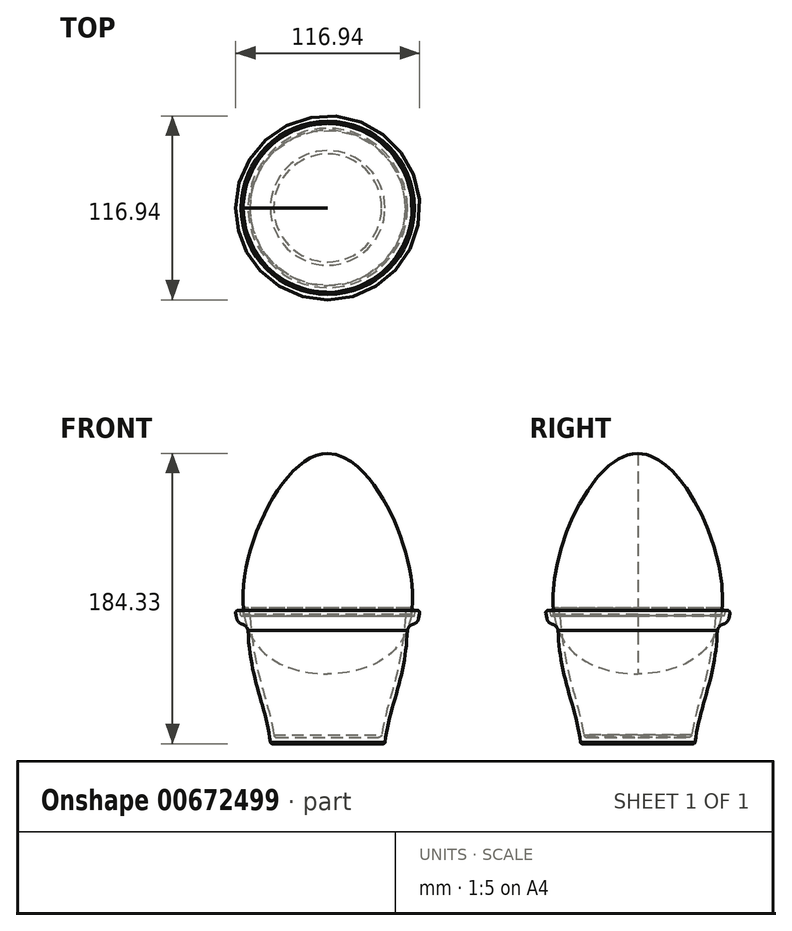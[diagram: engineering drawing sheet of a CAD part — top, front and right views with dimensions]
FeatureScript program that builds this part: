
annotation { "Feature Type Name" : "Feature", "Feature Type Description" : "" }
export const myFeature = defineFeature(function(context is Context, id is Id, definition is map)
    precondition{}
    {
        {
            var Q0;
            Q0=qCreatedBy(makeId("Front.planeOp"),FACE);
            var sketch = newSketch(context, id + "F0", { "sketchPlane" : qUnion([Q0])});
            skLineSegment(sketch, "E0", {"start": v(0, 0) * mm, "end": v(-47.5, 0) * mm});
            skLineSegment(sketch, "E1", {"start": v(-47.5, 0) * mm, "end": v(-32.5, -75) * mm});
            skLineSegment(sketch, "E2", {"start": v(-32.5, -75) * mm, "end": v(0, -75) * mm});
            skLineSegment(sketch, "E3", {"start": v(0, -75) * mm, "end": v(0, 0) * mm});
            skLineSegment(sketch, "E4.MirrorCS", {"start": v(0, 0) * mm, "end": v(47.5, 0) * mm});
            skLineSegment(sketch, "E5.MirrorCS", {"start": v(47.5, 0) * mm, "end": v(32.5, -75) * mm});
            skLineSegment(sketch, "E6.MirrorCS", {"start": v(32.5, -75) * mm, "end": v(0, -75) * mm});
            skSolve(sketch);
        }
        {
            var Q0;
            Q0=qCreatedBy(makeId("Front.planeOp"),FACE);
            var sketch = newSketch(context, id + "F1", { "sketchPlane" : qUnion([Q0])});
            skFitSpline(sketch, "E7", {"points": [v(0, 102.33) * mm, v(-53.18, 0) * mm, v(0, -37.67) * mm, v(53.18, 0) * mm, v(0, 102.33) * mm]});
            skLineSegment(sketch, "E8", {"start": v(-53.18, 0) * mm, "end": v(0, 0) * mm});
            skLineSegment(sketch, "E9", {"start": v(0, 102.33) * mm, "end": v(0, 0) * mm});
            skFitSpline(sketch, "E10", {"points": [v(-53.18, 0) * mm, v(0, -37.67) * mm, v(53.18, 0) * mm, v(0, 102.33) * mm, v(-53.18, 0) * mm]});
            skLineSegment(sketch, "E11", {"start": v(0, 0) * mm, "end": v(0, -37.67) * mm});
            skSolve(sketch);
        }
        {
            var Q0;
            Q0=qCreatedBy(makeId("Front.planeOp"),FACE);
            var sketch = newSketch(context, id + "F2", { "sketchPlane" : qUnion([Q0])});
            skLineSegment(sketch, "E12", {"start": v(-56.56, 2.58) * mm, "end": v(-56.97, 2.58) * mm});
            skLineSegment(sketch, "E13", {"start": v(-58.44, 0.79) * mm, "end": v(-57.82, -2.32) * mm});
            skLineSegment(sketch, "E14", {"start": v(-55.55, -6) * mm, "end": v(-54.6, -6) * mm});
            skLineSegment(sketch, "E15", {"start": v(-35.38, -82) * mm, "end": v(0, -82) * mm});
            skLineSegment(sketch, "E16", {"start": v(0, -82) * mm, "end": v(0, 0) * mm});
            skLineSegment(sketch, "E17", {"start": v(-55.58, 1.78) * mm, "end": v(-55.02, -1) * mm});
            skLineSegment(sketch, "E18", {"start": v(-55.02, -1) * mm, "end": v(-49.34, -1) * mm});
            skLineSegment(sketch, "E19", {"start": v(-32.3, -78) * mm, "end": v(0, -78) * mm});
            skPoint(sketch, "E20.visualSharp", {"position": v(-51.4, -6) * mm});
            skArc(sketch, "E20.filletArc", {"start": v(-50.6, -10.02) * mm, "mid": v(-51.85, -7.58) * mm, "end": v(-54.2, -6.17) * mm});
            skArc(sketch, "E21.filletArc", {"start": v(-57.82, -2.32) * mm, "mid": v(-56.56, -4.76) * mm, "end": v(-54.2, -6.17) * mm});
            skPoint(sketch, "E22.visualSharp", {"position": v(-36.2, -82) * mm});
            skArc(sketch, "E22.filletArc", {"start": v(-36.36, -81.2) * mm, "mid": v(-36.01, -81.77) * mm, "end": v(-35.38, -82) * mm});
            skPoint(sketch, "E23.visualSharp", {"position": v(-33.94, -78) * mm});
            skArc(sketch, "E23.filletArc", {"start": v(-34.26, -76.4) * mm, "mid": v(-33.57, -77.55) * mm, "end": v(-32.3, -78) * mm});
            skPoint(sketch, "E24.visualSharp", {"position": v(-58.8, 2.58) * mm});
            skArc(sketch, "E24.filletArc", {"start": v(-56.97, 2.58) * mm, "mid": v(-58.13, 2.03) * mm, "end": v(-58.44, 0.79) * mm});
            skPoint(sketch, "E25.visualSharp", {"position": v(-55.74, 2.58) * mm});
            skArc(sketch, "E25.filletArc", {"start": v(-55.58, 1.78) * mm, "mid": v(-55.93, 2.36) * mm, "end": v(-56.56, 2.58) * mm});
            skFitSpline(sketch, "E26", {"points": [v(-50.6, -10.02) * mm, v(-36.36, -81.2) * mm], "startDerivative": vector(3.36, -91.43) * mm, "endDerivative": vector(9.55, -72.68) * mm});
            skFitSpline(sketch, "E27", {"points": [v(-49.34, -1) * mm, v(-34.26, -76.4) * mm], "startDerivative": vector(8.58, -116.03) * mm, "endDerivative": vector(12.2, -75.01) * mm});
            skSolve(sketch);
        }
        {
            var Q0;
            Q0=makeQuery(id+"F2.imprint","IMPRINT",FACE,{"disambiguationData":[TD([[makeQuery(id+"F2.imprint","IMPRINT",EDGE,{"derivedFrom":sQuery(id+"F2.wireOp",EDGE,"E12")}),1.0]])]});
            var Q1;
            Q1=sQuery(id+"F0.wireOp",EDGE,"E3");
            revolve(context, id + "F3", {"entities" : qUnion([Q0]), "axis" : qUnion([Q1]), "revolveType" : RevolveType.FULL});
        }
        {
            var Q0;
            {var subQ0=sQuery(id+"F1.wireOp",EDGE,"E8");Q0=makeQuery(id+"F1.imprint","IMPRINT",FACE,{"disambiguationData":[TD([[makeQuery(id+"F1.imprint","IMPRINT",EDGE,{"derivedFrom":subQ0}),1.0]])]});}
            var Q1;
            {var subQ0=sQuery(id+"F1.wireOp",EDGE,"E8");Q1=makeQuery(id+"F1.imprint","IMPRINT",FACE,{"disambiguationData":[TD([[makeQuery(id+"F1.imprint","IMPRINT",EDGE,{"derivedFrom":subQ0}),-1.0]])]});}
            var Q2;
            Q2=sQuery(id+"F1.wireOp",EDGE,"E9");
            revolve(context, id + "F4", {"entities" : qUnion([Q0, Q1]), "axis" : qUnion([Q2]), "revolveType" : RevolveType.FULL});
        }
        {
            var Q0;
            Q0=qCreatedBy(makeId("Front.planeOp"),FACE);
            var sketch = newSketch(context, id + "F5", { "sketchPlane" : qUnion([Q0])});
            skLineSegment(sketch, "E28", {"start": v(-54.02, 3.23) * mm, "end": v(-53.42, -0.2) * mm});
            skLineSegment(sketch, "E29", {"start": v(-52.68, -0.82) * mm, "end": v(-50.2, -0.82) * mm});
            skLineSegment(sketch, "E30", {"start": v(-49.46, 0.06) * mm, "end": v(-50.06, 3.49) * mm});
            skLineSegment(sketch, "E31", {"start": v(-50.8, 4.1) * mm, "end": v(-53.28, 4.1) * mm});
            skPoint(sketch, "E32.visualSharp", {"position": v(-54.17, 4.1) * mm});
            skArc(sketch, "E32.filletArc", {"start": v(-53.28, 4.1) * mm, "mid": v(-53.85, 3.84) * mm, "end": v(-54.02, 3.23) * mm});
            skPoint(sketch, "E33.visualSharp", {"position": v(-50.17, 4.1) * mm});
            skArc(sketch, "E33.filletArc", {"start": v(-50.06, 3.49) * mm, "mid": v(-50.32, 3.93) * mm, "end": v(-50.8, 4.1) * mm});
            skPoint(sketch, "E34.visualSharp", {"position": v(-53.31, -0.82) * mm});
            skArc(sketch, "E34.filletArc", {"start": v(-53.42, -0.2) * mm, "mid": v(-53.16, -0.64) * mm, "end": v(-52.68, -0.82) * mm});
            skPoint(sketch, "E35.visualSharp", {"position": v(-49.31, -0.82) * mm});
            skArc(sketch, "E35.filletArc", {"start": v(-50.2, -0.82) * mm, "mid": v(-49.63, -0.55) * mm, "end": v(-49.46, 0.06) * mm});
            skSolve(sketch);
        }
        {
            var Q0;
            Q0=makeQuery(id+"F5.imprint","IMPRINT",FACE,{"disambiguationData":[TD([[makeQuery(id+"F5.imprint","IMPRINT",EDGE,{"derivedFrom":sQuery(id+"F5.wireOp",EDGE,"E28")}),1.0]])]});
            var Q1;
            Q1=sQuery(id+"F1.wireOp",EDGE,"E9");
            revolve(context, id + "F6", {"entities" : qUnion([Q0]), "axis" : qUnion([Q1]), "revolveType" : RevolveType.FULL});
        }
    });
